# Revit family: Zero Zone - RVMC30
name_source: partatom
category: Specialty Equipment
revit_build: Autodesk Revit Structure 2012 (Build: 20110622_0930(x64)
units: mm (PartAtom-declared; Revit-internal decimal feet)

## types (4) — shared parameters
Base Height = 3 1/2"
Comments = See Zero Zone Sales Spec Sheet
Description = Case, Cooler
Height with Elec Box = 83 5/8"
Manufacturer = Zero Zone
Plumbing = 1” PVC Drain
URL = www.zero-zone.com
Width = 39"
zero-valued in all types: Cost

## per-type parameters (varying)
| type | 2RVMC30 | 3RVMC30 | 4RVMC30 | 5RVMC30 | Description Legend | Glass | Length | Model |
| Zero Zone - 2RVMC30 | Yes | No | No | No | 2 Door Crystal Cooler, Cantilever | 2 | 62 1/8" | 2RVMC30 |
| Zero Zone - 3RVMC30 | No | Yes | No | No | 3 Door Crystal Cooler, Cantilever | 3 | 92 1/2" | 3RVMC30 |
| Zero Zone - 4RVMC30 | No | No | Yes | No | 4 Door Crystal Cooler, Cantilever | 4 | 123" | 4RVMC30 |
| Zero Zone - 5RVMC30 | No | No | No | Yes | 5 Door Crystal Cooler, Cantilever | 5 | 153 3/8" | 5RVMC30 |

## geometry (parser evidence)
native form markers: Sweep x3
no freeform markers — native parametric forms only
